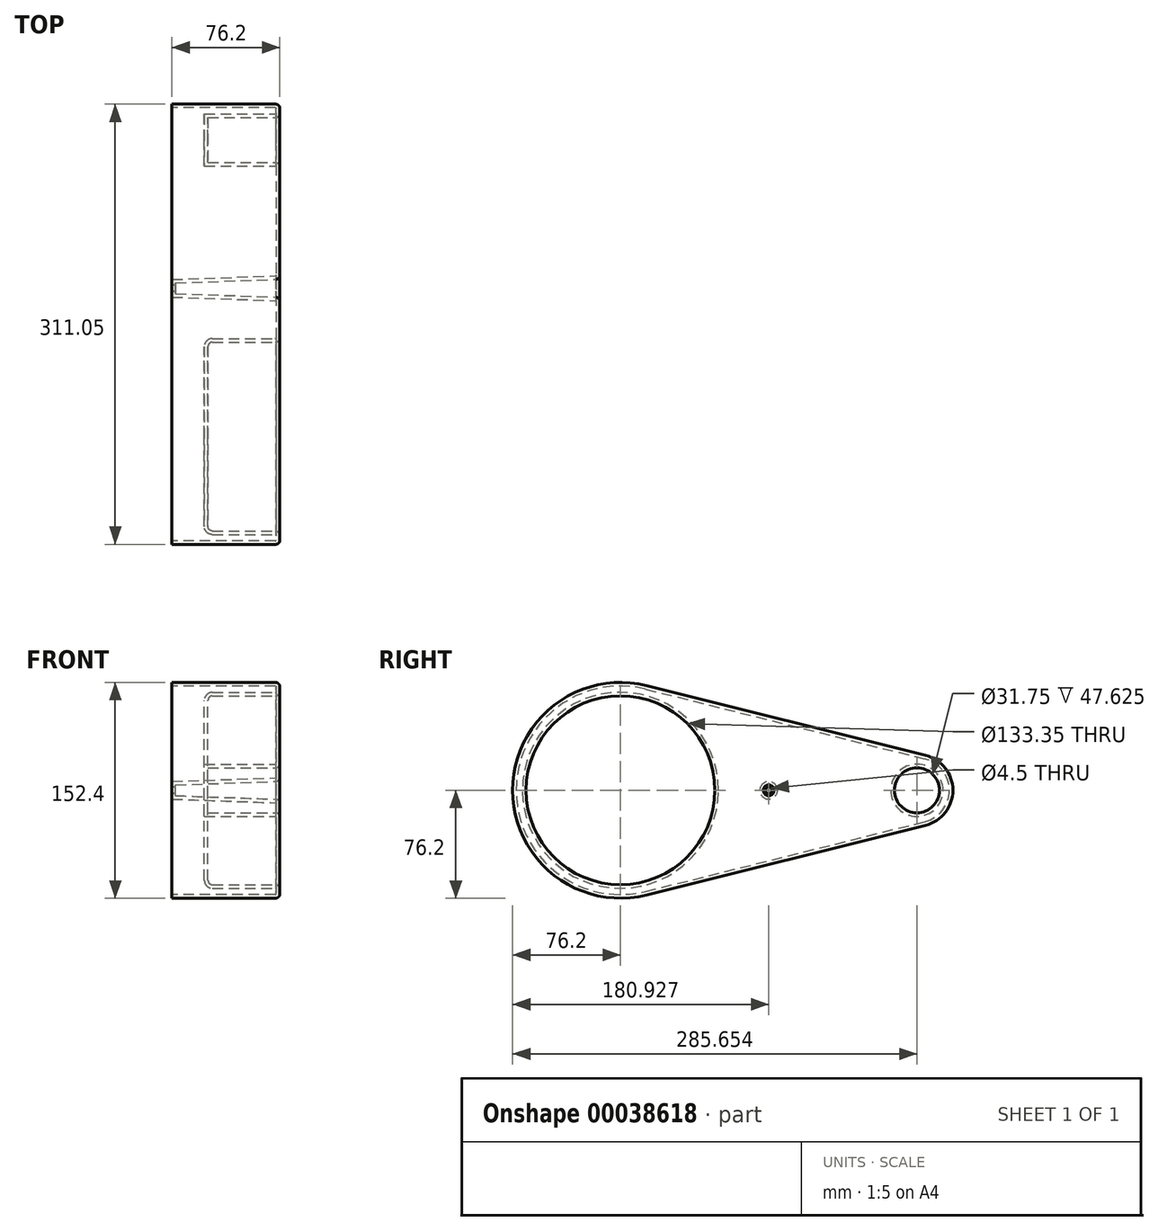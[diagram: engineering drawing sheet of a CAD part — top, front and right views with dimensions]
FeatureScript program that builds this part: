
annotation { "Feature Type Name" : "Feature", "Feature Type Description" : "" }
export const myFeature = defineFeature(function(context is Context, id is Id, definition is map)
    precondition{}
    {
        {
            var Q0;
            Q0=qCreatedBy(makeId("Right.planeOp"),FACE);
            var sketch = newSketch(context, id + "F0", { "sketchPlane" : qUnion([Q0])});
            skCircle(sketch, "E0", {"center": v(0, 0) * mm, "radius": 76.2 * mm});
            skCircle(sketch, "E1", {"center": v(209.45, 0) * mm, "radius": 25.4 * mm});
            skLineSegment(sketch, "E2", {"start": v(18.48, 73.92) * mm, "end": v(215.61, 24.64) * mm});
            skLineSegment(sketch, "E3", {"start": v(18.48, -73.92) * mm, "end": v(215.61, -24.64) * mm});
            skSolve(sketch);
        }
        {
            var Q0;
            {var subQ0=sQuery(id+"F0.wireOp",EDGE,"E1");var subQ1=makeQuery(id+"F0.imprint","INTERSECT",VERTEX,{"derivedFrom":[subQ0,sQuery(id+"F0.wireOp",EDGE,"E2")]});Q0=makeQuery(id+"F0.imprint","IMPRINT",FACE,{"disambiguationData":[TD([[makeQuery(id+"F0.imprint","IMPRINT",EDGE,{"disambiguationData":[TD([[subQ1,-1.0]])],"derivedFrom":subQ0}),1.0]])]});}
            var Q1;
            {var subQ0=sQuery(id+"F0.wireOp",EDGE,"E2");Q1=makeQuery(id+"F0.imprint","IMPRINT",FACE,{"disambiguationData":[TD([[makeQuery(id+"F0.imprint","IMPRINT",EDGE,{"derivedFrom":subQ0}),-1.0]])]});}
            var Q2;
            {var subQ0=sQuery(id+"F0.wireOp",EDGE,"E0");var subQ1=makeQuery(id+"F0.imprint","INTERSECT",VERTEX,{"derivedFrom":[subQ0,sQuery(id+"F0.wireOp",EDGE,"E2")]});Q2=makeQuery(id+"F0.imprint","IMPRINT",FACE,{"disambiguationData":[TD([[makeQuery(id+"F0.imprint","IMPRINT",EDGE,{"disambiguationData":[TD([[subQ1,-1.0]])],"derivedFrom":subQ0}),1.0]])]});}
            extrude(context, id + "F1", {"entities" : qUnion([Q0, Q1, Q2]), "depth" : 76.2 * mm});
        }
        {
            var Q0;
            Q0=makeQuery(id+"F1.opExtrude","CAP_FACE",FACE,{"disambiguationData":[OSD([sQuery(id+"F0.wireOp",EDGE,"E0"),sQuery(id+"F0.wireOp",EDGE,"E1"),sQuery(id+"F0.wireOp",EDGE,"E2"),sQuery(id+"F0.wireOp",EDGE,"E3")])],"isStart":false});
            var sketch = newSketch(context, id + "F2", { "sketchPlane" : qUnion([Q0])});
            skCircle(sketch, "E4", {"center": v(0, 0) * mm, "radius": 66.68 * mm});
            skCircle(sketch, "E5", {"center": v(209.45, 0) * mm, "radius": 15.88 * mm});
            skSolve(sketch);
        }
        {
            var Q0;
            Q0=makeQuery(id+"F2.imprint","IMPRINT",FACE,{"disambiguationData":[TD([[makeQuery(id+"F2.imprint","IMPRINT",EDGE,{"derivedFrom":sQuery(id+"F2.wireOp",EDGE,"E4")}),1.0]])]});
            var Q1;
            Q1=makeQuery(id+"F2.imprint","IMPRINT",FACE,{"disambiguationData":[TD([[makeQuery(id+"F2.imprint","IMPRINT",EDGE,{"derivedFrom":sQuery(id+"F2.wireOp",EDGE,"E5")}),1.0]])]});
            extrude(context, id + "F3", {"entities" : qUnion([Q0, Q1]), "operationType" : NewBodyOperationType.REMOVE, "oppositeDirection" : true, "depth" : 50.8 * mm});
        }
        {
            var Q0;
            Q0=makeQuery(id+"F1.opExtrude","CAP_FACE",FACE,{"disambiguationData":[OSD([sQuery(id+"F0.wireOp",EDGE,"E0"),sQuery(id+"F0.wireOp",EDGE,"E1"),sQuery(id+"F0.wireOp",EDGE,"E2"),sQuery(id+"F0.wireOp",EDGE,"E3")])],"isStart":false});
            var sketch = newSketch(context, id + "F4", { "sketchPlane" : qUnion([Q0])});
            skLineSegment(sketch, "E6", {"start": v(117.05, 49.28) * mm, "end": v(104.73, 0) * mm});
            skLineSegment(sketch, "E7", {"start": v(117.05, -49.28) * mm, "end": v(104.73, 0) * mm});
            skCircle(sketch, "E8", {"center": v(104.73, 0) * mm, "radius": 6.35 * mm});
            skSolve(sketch);
        }
        {
            var Q0;
            Q0 = qSketchRegion(id + "F4", true);
            extrude(context, id + "F5", {"entities" : qUnion([Q0]), "operationType" : NewBodyOperationType.REMOVE, "oppositeDirection" : true, "depth" : 73.66 * mm, "hasDraft" : true, "draftAngle" : 2 * degree, "draftPullDirection" : true});
        }
        {
            var Q0;
            Q0=makeQuery(id+"F1.opExtrude","CAP_FACE",FACE,{"disambiguationData":[OSD([sQuery(id+"F0.wireOp",EDGE,"E0"),sQuery(id+"F0.wireOp",EDGE,"E1"),sQuery(id+"F0.wireOp",EDGE,"E2"),sQuery(id+"F0.wireOp",EDGE,"E3")])],"isStart":false});
            var Q1;
            Q1=makeQuery(id+"F3.boolean.opBoolean","COPY",EDGE,{"derivedFrom":makeQuery(id+"F3.opExtrude","CAP_EDGE",EDGE,{"disambiguationData":[OSD([sQuery(id+"F2.wireOp",EDGE,"E4")])],"isStart":false})});
            fillet(context, id + "F6", {"entities" : qUnion([Q0, Q1]), "radius" : 3.17 * mm, "tangentPropagation" : true, "allowEdgeOverflow" : false});
        }
        {
            var Q0;
            Q0=makeQuery(id+"F1.opExtrude","CAP_FACE",FACE,{"disambiguationData":[OSD([sQuery(id+"F0.wireOp",EDGE,"E0"),sQuery(id+"F0.wireOp",EDGE,"E1"),sQuery(id+"F0.wireOp",EDGE,"E2"),sQuery(id+"F0.wireOp",EDGE,"E3")])],"isStart":true});
            shell(context, id + "F7", {"entities" : qUnion([Q0]), "thickness" : 2.54 * mm});
        }
        {
            var Q0;
            {var subQ0=sQuery(id+"F4.wireOp",EDGE,"E8");Q0=makeQuery(id+"F7.opShell","OFFSET_FACE",FACE,{"disambiguationData":[OSD([subQ0]),TDD([makeQuery(id+"F5.boolean.opBoolean","COPY",FACE,{"derivedFrom":makeQuery(id+"F5.opExtrude","CAP_FACE",FACE,{"disambiguationData":[OSD([subQ0])],"isStart":false})})])]});}
            var sketch = newSketch(context, id + "F8", { "sketchPlane" : qUnion([Q0])});
            skPoint(sketch, "E9", {"position": v(-104.73, 0) * mm});
            skSolve(sketch);
        }
        {
            var Q0;
            Q0=sQuery(id+"F8.wireOp",VERTEX,"E9");
            var Q1;
            Q1=makeQuery(id+"F1.opExtrude","SWEPT_BODY",BODY,{"disambiguationData":[OSD([sQuery(id+"F0.wireOp",EDGE,"E0"),sQuery(id+"F0.wireOp",EDGE,"E1"),sQuery(id+"F0.wireOp",EDGE,"E2"),sQuery(id+"F0.wireOp",EDGE,"E3")])]});
            hole(context, id + "F9", {"style" : HoleStyle.SIMPLE, "endStyle" : HoleEndStyle.THROUGH, "standardTappedOrClearance" : lookupTablePath({ "standard" : "ANSI", "fit" : "Normal (ASME)", "size" : "#8", "type" : "Clearance" }), "standardBlindInLast" : lookupTablePath({ "fit" : "Free", "standard" : "ANSI", "size" : "#8", "type" : "Clearance" }), "holeDiameter" : 4.5 * mm, "locations" : qUnion([Q0]), "scope" : qUnion([Q1]), "isTappedThrough" : true});
        }
    });
